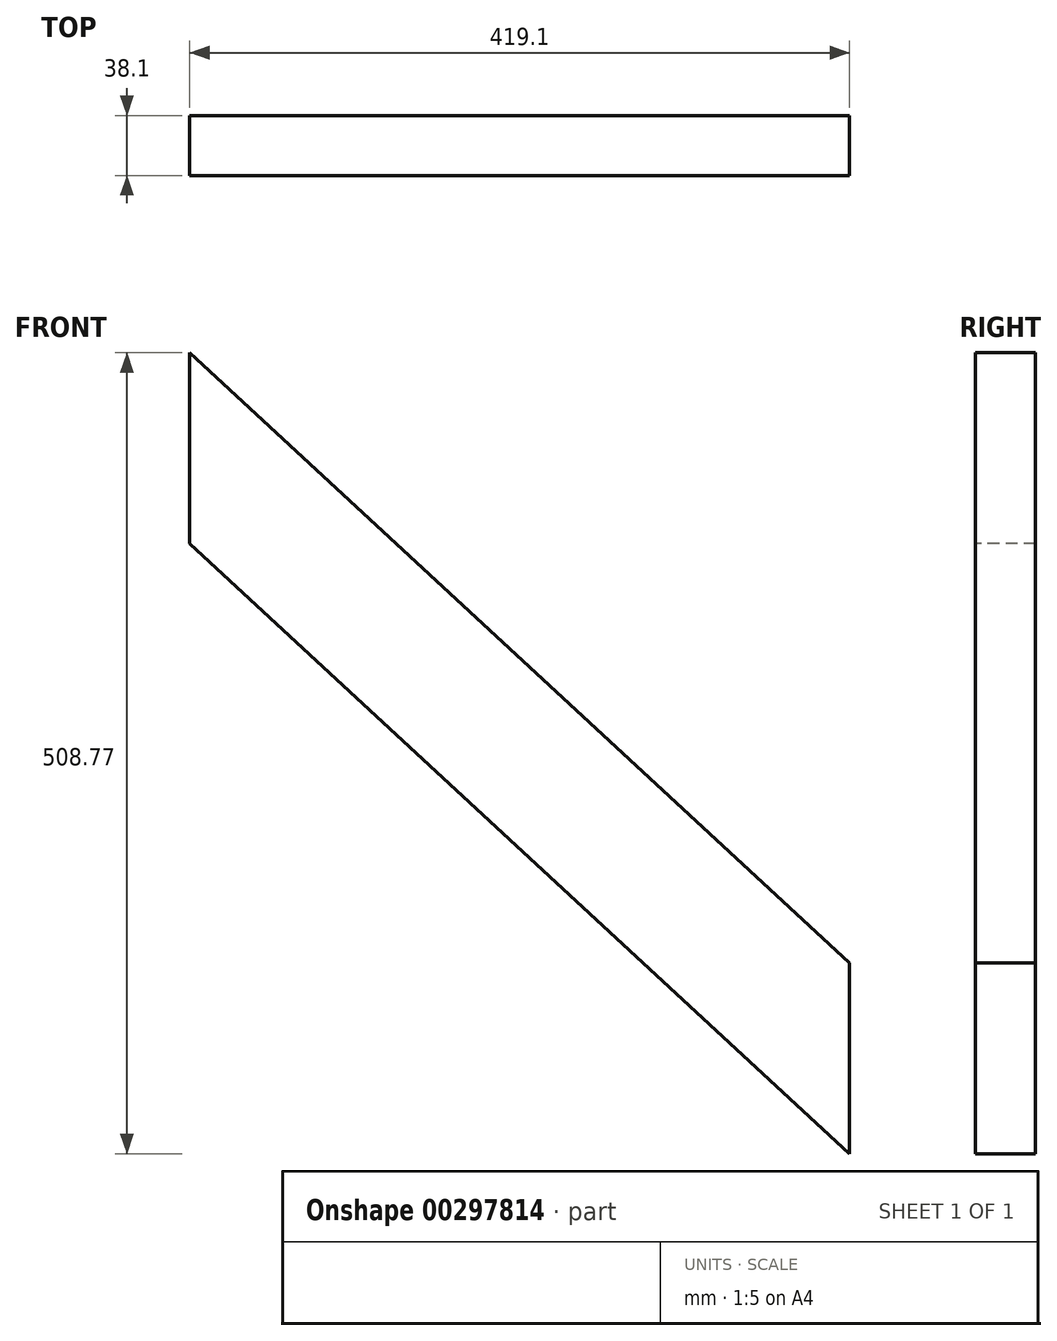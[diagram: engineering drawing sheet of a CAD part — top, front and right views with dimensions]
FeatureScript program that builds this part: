
annotation { "Feature Type Name" : "Feature", "Feature Type Description" : "" }
export const myFeature = defineFeature(function(context is Context, id is Id, definition is map)
    precondition{}
    {
        {
            var Q0;
            Q0=qCreatedBy(makeId("Front.planeOp"),FACE);
            var sketch = newSketch(context, id + "F0", { "sketchPlane" : qUnion([Q0])});
            skLineSegment(sketch, "E0.left", {"start": v(0, 0) * mm, "end": v(0, -121.1) * mm});
            skLineSegment(sketch, "E1", {"start": v(0, 0) * mm, "end": v(419.1, -387.67) * mm});
            skLineSegment(sketch, "E2", {"start": v(419.1, -508.77) * mm, "end": v(0, -121.1) * mm});
            skLineSegment(sketch, "E3", {"start": v(419.1, -387.67) * mm, "end": v(419.1, -508.77) * mm});
            skSolve(sketch);
        }
        {
            var Q0;
            Q0=makeQuery(id+"F0.imprint","IMPRINT",FACE,{"disambiguationData":[TD([[makeQuery(id+"F0.imprint","IMPRINT",EDGE,{"derivedFrom":sQuery(id+"F0.wireOp",EDGE,"E0.top")}),1.0]])]});
            var Q1;
            Q1=makeQuery(id+"F0.imprint","IMPRINT",FACE,{"disambiguationData":[TD([[makeQuery(id+"F0.imprint","IMPRINT",EDGE,{"derivedFrom":sQuery(id+"F0.wireOp",EDGE,"E0.left")}),1.0]])]});
            extrude(context, id + "F1", {"entities" : qUnion([Q0, Q1]), "oppositeDirection" : true, "depth" : 38.1 * mm});
        }
    });
